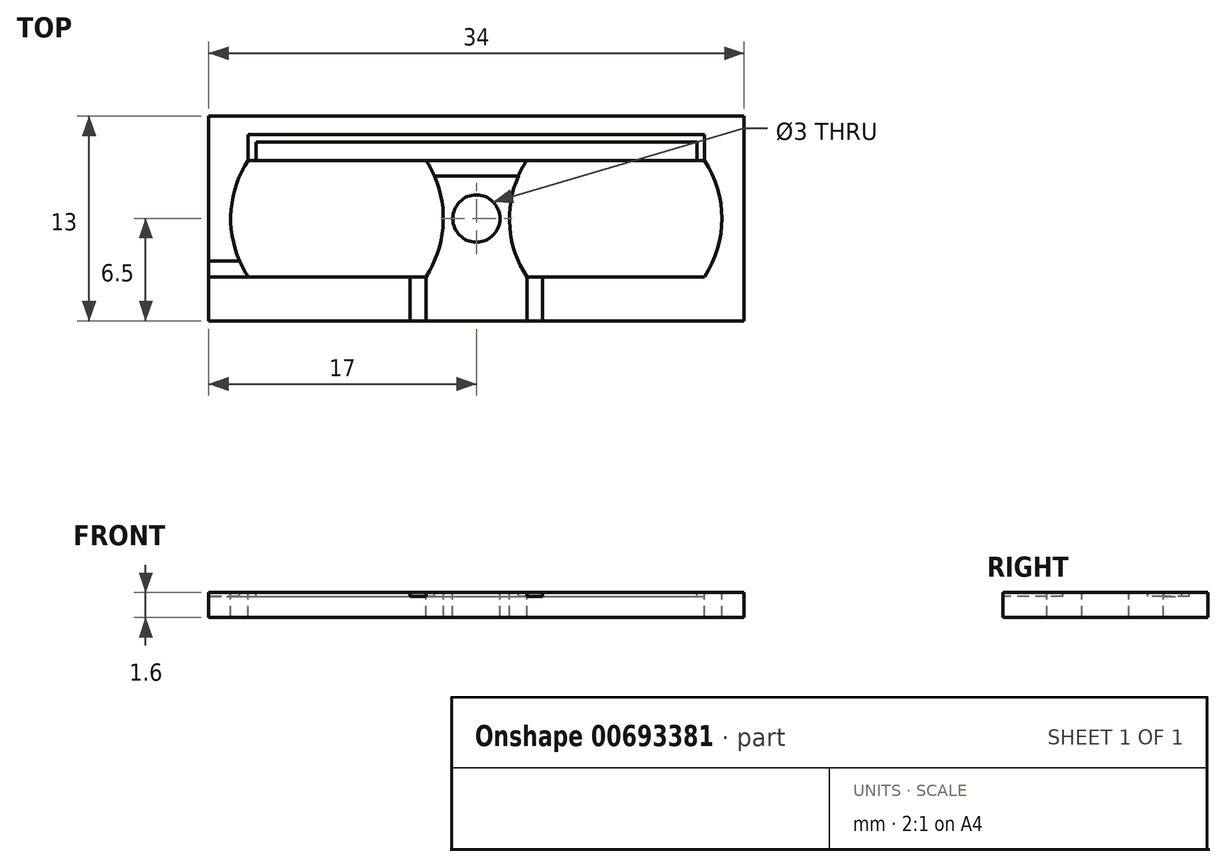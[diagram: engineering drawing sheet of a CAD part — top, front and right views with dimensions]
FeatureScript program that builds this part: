
annotation { "Feature Type Name" : "Feature", "Feature Type Description" : "" }
export const myFeature = defineFeature(function(context is Context, id is Id, definition is map)
    precondition{}
    {
        {
            var Q0;
            Q0=qCreatedBy(makeId("Top.planeOp"),FACE);
            var sketch = newSketch(context, id + "F0", { "sketchPlane" : qUnion([Q0])});
            skLineSegment(sketch, "E0.bottom", {"start": v(-17, 6.5) * mm, "end": v(17, 6.5) * mm});
            skLineSegment(sketch, "E0.top", {"start": v(-17, -6.5) * mm, "end": v(17, -6.5) * mm});
            skLineSegment(sketch, "E0.left", {"start": v(-17, 6.5) * mm, "end": v(-17, -6.5) * mm});
            skLineSegment(sketch, "E0.right", {"start": v(17, 6.5) * mm, "end": v(17, -6.5) * mm});
            skSolve(sketch);
        }
        {
            var Q0;
            Q0 = qSketchRegion(id + "F0", true);
            extrude(context, id + "F1", {"entities" : qUnion([Q0]), "depth" : 1.6 * mm, "offsetDistance" : 25 * mm});
        }
        {
            var Q0;
            Q0=makeQuery(id+"F1.opExtrude","CAP_FACE",FACE,{"disambiguationData":[OSD([sQuery(id+"F0.wireOp",EDGE,"E0.bottom"),sQuery(id+"F0.wireOp",EDGE,"E0.top"),sQuery(id+"F0.wireOp",EDGE,"E0.left"),sQuery(id+"F0.wireOp",EDGE,"E0.right")])],"isStart":false});
            var sketch = newSketch(context, id + "F2", { "sketchPlane" : qUnion([Q0])});
            skArc(sketch, "E1", {"start": v(-3.2, -3.7) * mm, "mid": v(-2.1, 0) * mm, "end": v(-3.2, 3.7) * mm});
            skArc(sketch, "E2", {"start": v(3.2, 3.7) * mm, "mid": v(2.1, 0) * mm, "end": v(3.2, -3.7) * mm});
            skCircle(sketch, "E3", {"center": v(-14.47, 0) * mm, "radius": 0.75 * mm});
            skCircle(sketch, "E4", {"center": v(-3.23, 0) * mm, "radius": 0.75 * mm});
            skCircle(sketch, "E5", {"center": v(3.23, 0) * mm, "radius": 0.75 * mm});
            skCircle(sketch, "E6", {"center": v(14.47, 0) * mm, "radius": 0.75 * mm});
            skLineSegment(sketch, "E7", {"start": v(-14.5, 3.7) * mm, "end": v(-3.2, 3.7) * mm});
            skLineSegment(sketch, "E8", {"start": v(-14.5, -3.7) * mm, "end": v(-3.2, -3.7) * mm});
            skLineSegment(sketch, "E9.trimOffspring", {"start": v(3.2, 3.7) * mm, "end": v(14.5, 3.7) * mm});
            skLineSegment(sketch, "E10.trimOffspring", {"start": v(3.2, -3.7) * mm, "end": v(14.5, -3.7) * mm});
            skArc(sketch, "E11.trimOffspring", {"start": v(-14.5, 3.7) * mm, "mid": v(-15.6, 0) * mm, "end": v(-14.5, -3.7) * mm});
            skArc(sketch, "E12.trimOffspring", {"start": v(14.5, -3.7) * mm, "mid": v(15.6, 0) * mm, "end": v(14.5, 3.7) * mm});
            skSolve(sketch);
        }
        {
            var Q0;
            Q0=makeQuery(id+"F2.imprint","IMPRINT",FACE,{"disambiguationData":[TD([[makeQuery(id+"F2.imprint","IMPRINT",EDGE,{"derivedFrom":sQuery(id+"F2.wireOp",EDGE,"E1")}),1.0]])]});
            var Q1;
            Q1=makeQuery(id+"F2.imprint","IMPRINT",FACE,{"disambiguationData":[TD([[makeQuery(id+"F2.imprint","IMPRINT",EDGE,{"derivedFrom":sQuery(id+"F2.wireOp",EDGE,"E2")}),1.0]])]});
            var Q2;
            Q2=makeQuery(id+"F2.imprint","IMPRINT",FACE,{"disambiguationData":[TD([[makeQuery(id+"F2.imprint","IMPRINT",EDGE,{"derivedFrom":sQuery(id+"F2.wireOp",EDGE,"E4")}),1.0]])]});
            var Q3;
            Q3=makeQuery(id+"F2.imprint","IMPRINT",FACE,{"disambiguationData":[TD([[makeQuery(id+"F2.imprint","IMPRINT",EDGE,{"derivedFrom":sQuery(id+"F2.wireOp",EDGE,"E3")}),1.0]])]});
            var Q4;
            Q4=makeQuery(id+"F2.imprint","IMPRINT",FACE,{"disambiguationData":[TD([[makeQuery(id+"F2.imprint","IMPRINT",EDGE,{"derivedFrom":sQuery(id+"F2.wireOp",EDGE,"E5")}),1.0]])]});
            var Q5;
            Q5=makeQuery(id+"F2.imprint","IMPRINT",FACE,{"disambiguationData":[TD([[makeQuery(id+"F2.imprint","IMPRINT",EDGE,{"derivedFrom":sQuery(id+"F2.wireOp",EDGE,"E6")}),1.0]])]});
            extrude(context, id + "F3", {"entities" : qUnion([Q0, Q1, Q2, Q3, Q4, Q5]), "operationType" : NewBodyOperationType.REMOVE, "endBound" : BoundingType.THROUGH_ALL, "oppositeDirection" : true, "depth" : 25 * mm, "offsetDistance" : 25 * mm});
        }
        {
            var Q0;
            Q0=makeQuery(id+"F1.opExtrude","CAP_FACE",FACE,{"disambiguationData":[OSD([sQuery(id+"F0.wireOp",EDGE,"E0.bottom"),sQuery(id+"F0.wireOp",EDGE,"E0.top"),sQuery(id+"F0.wireOp",EDGE,"E0.left"),sQuery(id+"F0.wireOp",EDGE,"E0.right")])],"isStart":false});
            var sketch = newSketch(context, id + "F4", { "sketchPlane" : qUnion([Q0])});
            skCircle(sketch, "E13", {"center": v(0, 0) * mm, "radius": 1.5 * mm});
            skSolve(sketch);
        }
        {
            var Q0;
            Q0=makeQuery(id+"F4.imprint","IMPRINT",FACE,{"disambiguationData":[TD([[makeQuery(id+"F4.imprint","IMPRINT",EDGE,{"derivedFrom":sQuery(id+"F4.wireOp",EDGE,"E13")}),1.0]])]});
            extrude(context, id + "F5", {"entities" : qUnion([Q0]), "operationType" : NewBodyOperationType.REMOVE, "endBound" : BoundingType.THROUGH_ALL, "oppositeDirection" : true, "depth" : 25 * mm, "offsetDistance" : 25 * mm});
        }
        {
            var Q0;
            Q0=makeQuery(id+"F1.opExtrude","CAP_FACE",FACE,{"disambiguationData":[OSD([sQuery(id+"F0.wireOp",EDGE,"E0.bottom"),sQuery(id+"F0.wireOp",EDGE,"E0.top"),sQuery(id+"F0.wireOp",EDGE,"E0.left"),sQuery(id+"F0.wireOp",EDGE,"E0.right")])],"isStart":false});
            var sketch = newSketch(context, id + "F6", { "sketchPlane" : qUnion([Q0])});
            skLineSegment(sketch, "E14", {"start": v(-17, -3.7) * mm, "end": v(-14.5, -3.7) * mm});
            skLineSegment(sketch, "E15", {"start": v(-15.04, -2.7) * mm, "end": v(-17, -2.7) * mm});
            skLineSegment(sketch, "E16.left", {"start": v(-4.2, -3.7) * mm, "end": v(-4.2, -6.5) * mm});
            skLineSegment(sketch, "E16.right", {"start": v(-3.2, -3.7) * mm, "end": v(-3.2, -6.5) * mm});
            skLineSegment(sketch, "E17.left", {"start": v(3.2, -3.7) * mm, "end": v(3.2, -6.5) * mm});
            skLineSegment(sketch, "E17.right", {"start": v(4.2, -3.7) * mm, "end": v(4.2, -6.5) * mm});
            skLineSegment(sketch, "E18.top", {"start": v(-14, 4.85) * mm, "end": v(14, 4.85) * mm});
            skLineSegment(sketch, "E18.left", {"start": v(-14, 3.7) * mm, "end": v(-14, 4.85) * mm});
            skLineSegment(sketch, "E18.right", {"start": v(14, 3.7) * mm, "end": v(14, 4.85) * mm});
            skLineSegment(sketch, "E19", {"start": v(-14.5, 3.7) * mm, "end": v(-14.5, 5.35) * mm});
            skLineSegment(sketch, "E20", {"start": v(-14.5, 5.35) * mm, "end": v(14.5, 5.35) * mm});
            skLineSegment(sketch, "E21", {"start": v(14.5, 5.35) * mm, "end": v(14.5, 3.7) * mm});
            skPoint(sketch, "E22", {"position": v(9.8, 3.7) * mm});
            skLineSegment(sketch, "E23", {"start": v(-3.2, 3.7) * mm, "end": v(3.2, 3.7) * mm});
            skLineSegment(sketch, "E24", {"start": v(-2.66, 2.7) * mm, "end": v(2.66, 2.7) * mm});
            skSolve(sketch);
        }
        {
            var Q0;
            {var subQ0=sQuery(id+"F6.wireOp",EDGE,"E16.left");Q0=makeQuery(id+"F6.imprint","IMPRINT",FACE,{"disambiguationData":[TD([[makeQuery(id+"F6.imprint","IMPRINT",EDGE,{"derivedFrom":subQ0}),1.0]])]});}
            var Q1;
            {var subQ0=sQuery(id+"F6.wireOp",EDGE,"E14");Q1=makeQuery(id+"F6.imprint","IMPRINT",FACE,{"disambiguationData":[TD([[makeQuery(id+"F6.imprint","IMPRINT",EDGE,{"derivedFrom":subQ0}),1.0]])]});}
            var Q2;
            {var subQ0=sQuery(id+"F6.wireOp",EDGE,"E17.left");Q2=makeQuery(id+"F6.imprint","IMPRINT",FACE,{"disambiguationData":[TD([[makeQuery(id+"F6.imprint","IMPRINT",EDGE,{"derivedFrom":subQ0}),1.0]])]});}
            var Q3;
            Q3=makeQuery(id+"F6.imprint","IMPRINT",FACE,{"disambiguationData":[TD([[makeQuery(id+"F6.imprint","IMPRINT",EDGE,{"derivedFrom":sQuery(id+"F6.wireOp",EDGE,"E18.top")}),1.0]])]});
            var Q4;
            {var subQ0=sQuery(id+"F6.wireOp",EDGE,"E23");Q4=makeQuery(id+"F6.imprint","IMPRINT",FACE,{"disambiguationData":[TD([[makeQuery(id+"F6.imprint","IMPRINT",EDGE,{"derivedFrom":subQ0}),-1.0]])]});}
            extrude(context, id + "F7", {"entities" : qUnion([Q0, Q1, Q2, Q3, Q4]), "operationType" : NewBodyOperationType.REMOVE, "oppositeDirection" : true, "depth" : .25 * mm, "offsetDistance" : 25 * mm});
        }
    });
